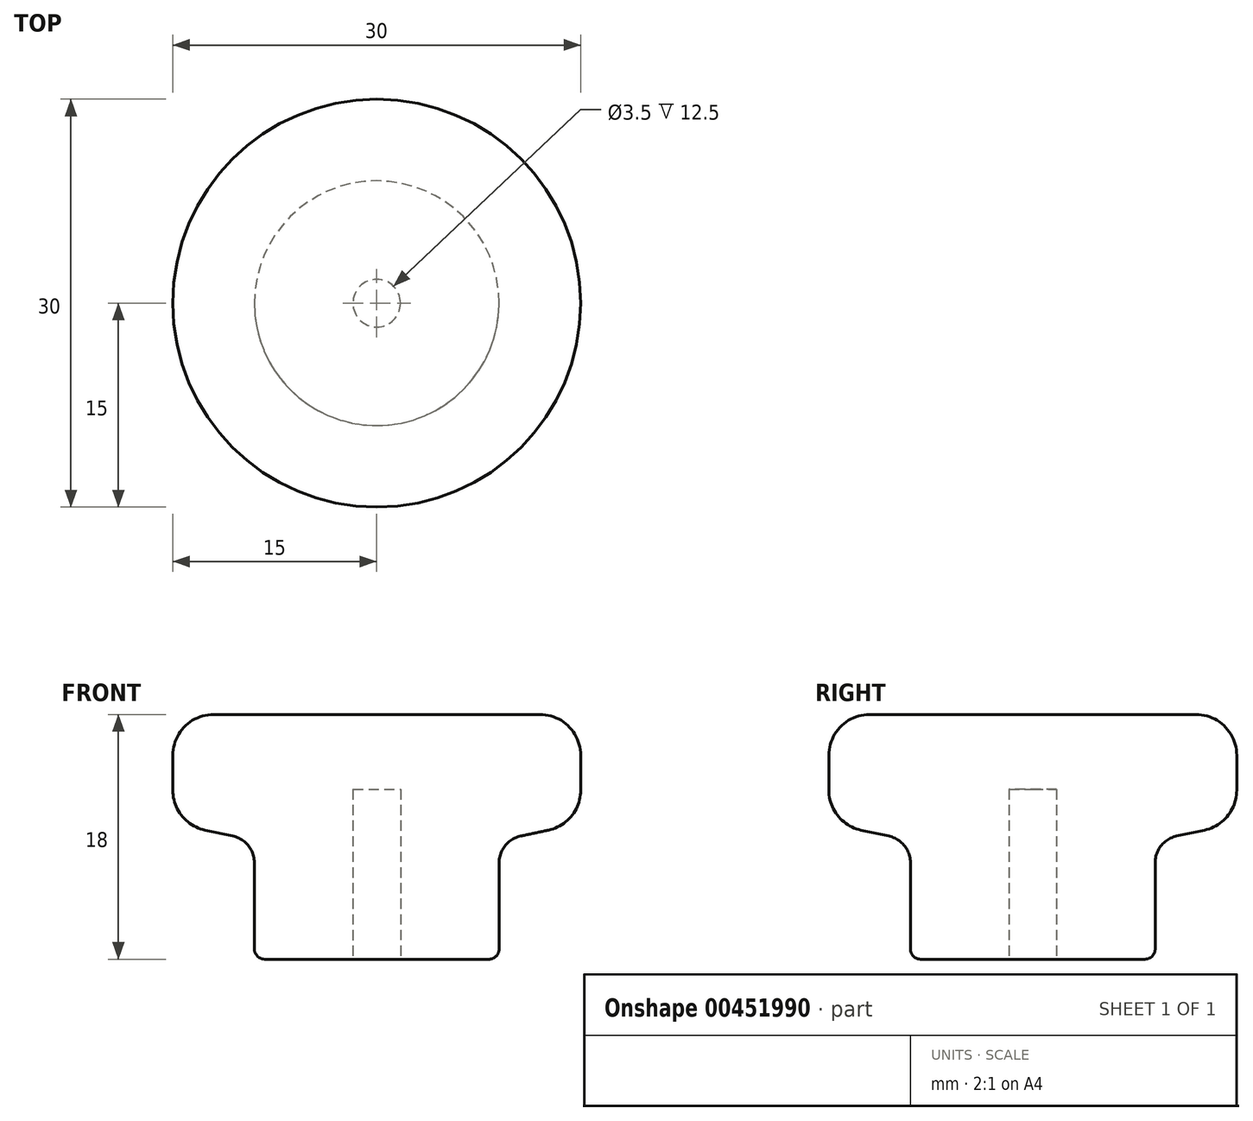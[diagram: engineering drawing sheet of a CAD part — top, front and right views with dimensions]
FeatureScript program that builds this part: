
annotation { "Feature Type Name" : "Feature", "Feature Type Description" : "" }
export const myFeature = defineFeature(function(context is Context, id is Id, definition is map)
    precondition{}
    {
        {
            var Q0;
            Q0=qCreatedBy(makeId("Front.planeOp"),FACE);
            var sketch = newSketch(context, id + "F0", { "sketchPlane" : qUnion([Q0])});
            skLineSegment(sketch, "E0", {"start": v(0, 0) * mm, "end": v(0, 18) * mm});
            skLineSegment(sketch, "E1", {"start": v(0, 18) * mm, "end": v(-15, 18) * mm});
            skLineSegment(sketch, "E2", {"start": v(-15, 18) * mm, "end": v(-15, 10) * mm});
            skLineSegment(sketch, "E3", {"start": v(-15, 10) * mm, "end": v(-9, 8.72) * mm});
            skLineSegment(sketch, "E4", {"start": v(-9, 8.72) * mm, "end": v(-9, 0) * mm});
            skLineSegment(sketch, "E5", {"start": v(-9, 0) * mm, "end": v(0, 0) * mm});
            skSolve(sketch);
        }
        {
            var Q0;
            Q0=makeQuery(id+"F0.imprint","IMPRINT",FACE,{"disambiguationData":[TD([[makeQuery(id+"F0.imprint","IMPRINT",EDGE,{"derivedFrom":sQuery(id+"F0.wireOp",EDGE,"E0")}),1.0]])]});
            var Q1;
            Q1=sQuery(id+"F0.wireOp",EDGE,"E0");
            revolve(context, id + "F1", {"entities" : qUnion([Q0]), "axis" : qUnion([Q1]), "revolveType" : RevolveType.FULL});
        }
        {
            var Q0;
            Q0=makeQuery(id+"F1.opRevolve","SWEPT_FACE",FACE,{"disambiguationData":[OSD([sQuery(id+"F0.wireOp",EDGE,"E5")])]});
            var sketch = newSketch(context, id + "F2", { "sketchPlane" : qUnion([Q0])});
            skCircle(sketch, "E6", {"center": v(0, 0) * mm, "radius": 1.75 * mm});
            skSolve(sketch);
        }
        {
            var Q0;
            Q0 = qSketchRegion(id + "F2", true);
            extrude(context, id + "F3", {"entities" : qUnion([Q0]), "operationType" : NewBodyOperationType.REMOVE, "oppositeDirection" : true, "depth" : 12.5 * mm});
        }
        {
            var Q0;
            Q0=makeQuery(id+"F1.opRevolve","SWEPT_FACE",FACE,{"disambiguationData":[OSD([sQuery(id+"F0.wireOp",EDGE,"E1")])]});
            var Q1;
            Q1=makeQuery(id+"F1.opRevolve","SWEPT_EDGE",EDGE,{"disambiguationData":[OSD([sQuery(id+"F0.wireOp",EDGE,"E2"),sQuery(id+"F0.wireOp",EDGE,"E3")])]});
            fillet(context, id + "F4", {"entities" : qUnion([Q0, Q1]), "radius" : 3 * mm, "tangentPropagation" : true, "allowEdgeOverflow" : false});
        }
        {
            var Q0;
            Q0=makeQuery(id+"F1.opRevolve","SWEPT_EDGE",EDGE,{"disambiguationData":[OSD([sQuery(id+"F0.wireOp",EDGE,"E3"),sQuery(id+"F0.wireOp",EDGE,"E4")])]});
            fillet(context, id + "F5", {"entities" : qUnion([Q0]), "radius" : 2 * mm, "tangentPropagation" : true, "allowEdgeOverflow" : false});
        }
        {
            var Q0;
            Q0=makeQuery(id+"F1.opRevolve","SWEPT_EDGE",EDGE,{"disambiguationData":[OSD([sQuery(id+"F0.wireOp",EDGE,"E4"),sQuery(id+"F0.wireOp",EDGE,"E5")])]});
            fillet(context, id + "F6", {"entities" : qUnion([Q0]), "radius" : .75 * mm, "tangentPropagation" : true, "allowEdgeOverflow" : false});
        }
    });
